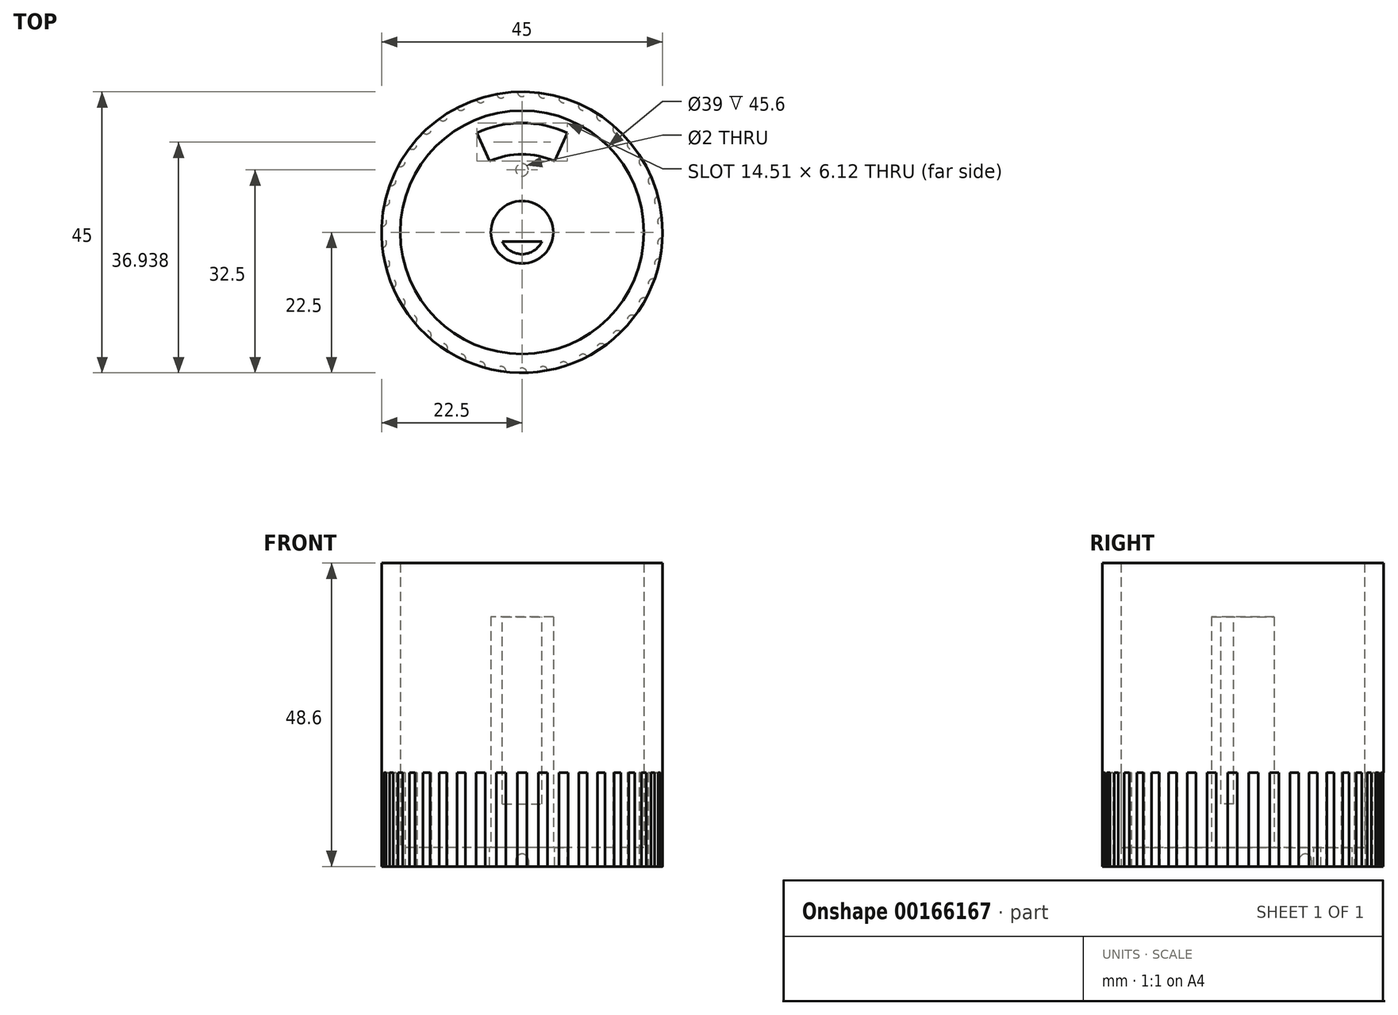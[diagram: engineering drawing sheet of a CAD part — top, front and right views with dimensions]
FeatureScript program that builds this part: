
annotation { "Feature Type Name" : "Feature", "Feature Type Description" : "" }
export const myFeature = defineFeature(function(context is Context, id is Id, definition is map)
    precondition{}
    {
        {
            var Q0;
            Q0=qCreatedBy(makeId("Top.planeOp"),FACE);
            var sketch = newSketch(context, id + "F10", { "sketchPlane" : qUnion([Q0])});
            skCircle(sketch, "E0", {"center": v(0, 0) * mm, "radius": 22.5 * mm});
            skSolve(sketch);
        }
        {
            var Q0;
            Q0=makeQuery(id+"F10.imprint","IMPRINT",FACE,{"disambiguationData":[TD([[makeQuery(id+"F10.imprint","IMPRINT",EDGE,{"derivedFrom":sQuery(id+"F10.wireOp",EDGE,"E0")}),1.0]])]});
            extrude(context, id + "F0", {"entities" : qUnion([Q0]), "depth" : 48.6 * mm});
        }
        {
            var Q0;
            Q0=makeQuery(id+"F0.opExtrude","CAP_FACE",FACE,{"disambiguationData":[OSD([sQuery(id+"F10.wireOp",EDGE,"E0")])],"isStart":false});
            shell(context, id + "F1", {"entities" : qUnion([Q0]), "thickness" : 3 * mm});
        }
        {
            var Q0;
            {var subQ0=sQuery(id+"F10.wireOp",EDGE,"E0");Q0=makeQuery(id+"F1.opShell","OFFSET_FACE",FACE,{"disambiguationData":[OSD([subQ0]),TDD([makeQuery(id+"F0.opExtrude","CAP_FACE",FACE,{"disambiguationData":[OSD([subQ0])],"isStart":true})])]});}
            var sketch = newSketch(context, id + "F2", { "sketchPlane" : qUnion([Q0])});
            skCircle(sketch, "E1", {"center": v(0, 0) * mm, "radius": 5 * mm});
            skSolve(sketch);
        }
        {
            var Q0;
            Q0 = qSketchRegion(id + "F2", true);
            extrude(context, id + "F3", {"entities" : qUnion([Q0]), "operationType" : NewBodyOperationType.ADD, "depth" : 37 * mm});
        }
        {
            var Q0;
            Q0=makeQuery(id+"F3.opExtrude","CAP_FACE",FACE,{"disambiguationData":[OSD([sQuery(id+"F2.wireOp",EDGE,"E1")])],"isStart":false});
            var sketch = newSketch(context, id + "F4", { "sketchPlane" : qUnion([Q0])});
            skCircle(sketch, "E2", {"center": v(0, 0) * mm, "radius": 3.5 * mm});
            skPoint(sketch, "E3", {"position": v(0, 3.5) * mm});
            skLineSegment(sketch, "E4", {"start": v(-3.9, -1.5) * mm, "end": v(4, -1.5) * mm});
            skSolve(sketch);
        }
        {
            var Q0;
            {var subQ0=sQuery(id+"F4.wireOp",EDGE,"E4");var subQ1=sQuery(id+"F4.wireOp",EDGE,"E2");var subQ2=makeQuery(id+"F4.imprint","INTERSECT",VERTEX,{"disambiguationData":[OD(0.0)],"derivedFrom":[subQ1,subQ0]});Q0=makeQuery(id+"F4.imprint","IMPRINT",FACE,{"disambiguationData":[TD([[makeQuery(id+"F4.imprint","IMPRINT",EDGE,{"disambiguationData":[TD([[subQ2,1.0]])],"derivedFrom":subQ1}),1.0]])]});}
            extrude(context, id + "F11", {"entities" : qUnion([Q0]), "operationType" : NewBodyOperationType.REMOVE, "oppositeDirection" : true, "depth" : 30 * mm});
        }
        {
            var Q0;
            {var subQ0=sQuery(id+"F10.wireOp",EDGE,"E0");Q0=makeQuery(id+"F1.opShell","OFFSET_FACE",FACE,{"disambiguationData":[OSD([subQ0]),TDD([makeQuery(id+"F0.opExtrude","CAP_FACE",FACE,{"disambiguationData":[OSD([subQ0])],"isStart":true})])]});}
            var sketch = newSketch(context, id + "F12", { "sketchPlane" : qUnion([Q0])});
            skCircle(sketch, "E5", {"center": v(0, 0) * mm, "radius": 17.5 * mm});
            skCircle(sketch, "E6", {"center": v(0, 0) * mm, "radius": 12.5 * mm});
            skLineSegment(sketch, "E7", {"start": v(0, 0) * mm, "end": v(7.26, 15.93) * mm});
            skLineSegment(sketch, "E8", {"start": v(0, 0) * mm, "end": v(-7.26, 15.93) * mm});
            skLineSegment(sketch, "E9", {"start": v(-7.26, 15.93) * mm, "end": v(7.26, 15.93) * mm});
            skSolve(sketch);
        }
        {
            var Q0;
            {var subQ5=sQuery(id+"F12.wireOp",EDGE,"E9");Q0=makeQuery(id+"F12.imprint","IMPRINT",FACE,{"disambiguationData":[TD([[makeQuery(id+"F12.imprint","IMPRINT",EDGE,{"derivedFrom":subQ5}),-1.0]])]});}
            var Q1;
            {var subQ0=sQuery(id+"F12.wireOp",EDGE,"E9");Q1=makeQuery(id+"F12.imprint","IMPRINT",FACE,{"disambiguationData":[TD([[makeQuery(id+"F12.imprint","IMPRINT",EDGE,{"derivedFrom":subQ0}),1.0]])]});}
            extrude(context, id + "F5", {"entities" : qUnion([Q0, Q1]), "operationType" : NewBodyOperationType.REMOVE, "oppositeDirection" : true, "depth" : 25 * mm});
        }
        {
            var Q0;
            Q0=makeQuery(id+"F0.opExtrude","CAP_FACE",FACE,{"disambiguationData":[OSD([sQuery(id+"F10.wireOp",EDGE,"E0")])],"isStart":true});
            var sketch = newSketch(context, id + "F13", { "sketchPlane" : qUnion([Q0])});
            skCircle(sketch, "E10", {"center": v(0, -10) * mm, "radius": 1 * mm});
            skSolve(sketch);
        }
        {
            var Q0;
            Q0=makeQuery(id+"F13.imprint","IMPRINT",FACE,{"disambiguationData":[TD([[makeQuery(id+"F13.imprint","IMPRINT",EDGE,{"derivedFrom":sQuery(id+"F13.wireOp",EDGE,"E10")}),1.0]])]});
            extrude(context, id + "F6", {"entities" : qUnion([Q0]), "operationType" : NewBodyOperationType.REMOVE, "oppositeDirection" : true, "depth" : 2 * mm});
        }
        {
            var Q0;
            Q0=makeQuery(id+"F6.boolean.opBoolean","COPY",EDGE,{"derivedFrom":makeQuery(id+"F6.opExtrude","CAP_EDGE",EDGE,{"disambiguationData":[OSD([sQuery(id+"F13.wireOp",EDGE,"E10")])],"isStart":false})});
            fillet(context, id + "F7", {"entities" : qUnion([Q0]), "radius" : 1 * mm, "tangentPropagation" : true, "allowEdgeOverflow" : false});
        }
        {
            var Q0;
            Q0=makeQuery(id+"F0.opExtrude","CAP_FACE",FACE,{"disambiguationData":[OSD([sQuery(id+"F10.wireOp",EDGE,"E0")])],"isStart":true});
            var sketch = newSketch(context, id + "F8", { "sketchPlane" : qUnion([Q0])});
            skCircle(sketch, "E11", {"center": v(0, -22.5) * mm, "radius": 0.75 * mm});
            skCircle(sketch, "E12.1.0", {"center": v(3.35, -22.25) * mm, "radius": 0.75 * mm});
            skCircle(sketch, "E12.2.0", {"center": v(6.63, -21.5) * mm, "radius": 0.75 * mm});
            skCircle(sketch, "E12.3.0", {"center": v(9.76, -20.27) * mm, "radius": 0.75 * mm});
            skCircle(sketch, "E12.4.0", {"center": v(12.67, -18.6) * mm, "radius": 0.75 * mm});
            skCircle(sketch, "E12.5.0", {"center": v(15.3, -16.5) * mm, "radius": 0.75 * mm});
            skCircle(sketch, "E12.6.0", {"center": v(17.6, -14.03) * mm, "radius": 0.75 * mm});
            skCircle(sketch, "E12.7.0", {"center": v(19.49, -11.25) * mm, "radius": 0.75 * mm});
            skCircle(sketch, "E12.8.0", {"center": v(20.94, -8.22) * mm, "radius": 0.75 * mm});
            skCircle(sketch, "E12.9.0", {"center": v(21.94, -5) * mm, "radius": 0.75 * mm});
            skCircle(sketch, "E12.10.0", {"center": v(22.44, -1.68) * mm, "radius": 0.75 * mm});
            skCircle(sketch, "E12.11.0", {"center": v(22.44, 1.68) * mm, "radius": 0.75 * mm});
            skCircle(sketch, "E12.12.0", {"center": v(21.94, 5) * mm, "radius": 0.75 * mm});
            skCircle(sketch, "E12.13.0", {"center": v(20.94, 8.22) * mm, "radius": 0.75 * mm});
            skCircle(sketch, "E12.14.0", {"center": v(19.49, 11.25) * mm, "radius": 0.75 * mm});
            skCircle(sketch, "E12.15.0", {"center": v(17.6, 14.03) * mm, "radius": 0.75 * mm});
            skCircle(sketch, "E12.16.0", {"center": v(15.3, 16.5) * mm, "radius": 0.75 * mm});
            skCircle(sketch, "E12.17.0", {"center": v(12.67, 18.6) * mm, "radius": 0.75 * mm});
            skCircle(sketch, "E12.18.0", {"center": v(9.76, 20.27) * mm, "radius": 0.75 * mm});
            skCircle(sketch, "E12.19.0", {"center": v(6.63, 21.5) * mm, "radius": 0.75 * mm});
            skCircle(sketch, "E12.20.0", {"center": v(3.35, 22.25) * mm, "radius": 0.75 * mm});
            skCircle(sketch, "E12.21.0", {"center": v(0, 22.5) * mm, "radius": 0.75 * mm});
            skCircle(sketch, "E12.22.0", {"center": v(-3.35, 22.25) * mm, "radius": 0.75 * mm});
            skCircle(sketch, "E12.23.0", {"center": v(-6.63, 21.5) * mm, "radius": 0.75 * mm});
            skCircle(sketch, "E12.24.0", {"center": v(-9.76, 20.27) * mm, "radius": 0.75 * mm});
            skCircle(sketch, "E12.25.0", {"center": v(-12.67, 18.6) * mm, "radius": 0.75 * mm});
            skCircle(sketch, "E12.26.0", {"center": v(-15.3, 16.5) * mm, "radius": 0.75 * mm});
            skCircle(sketch, "E12.27.0", {"center": v(-17.6, 14.03) * mm, "radius": 0.75 * mm});
            skCircle(sketch, "E12.28.0", {"center": v(-19.49, 11.25) * mm, "radius": 0.75 * mm});
            skCircle(sketch, "E12.29.0", {"center": v(-20.94, 8.22) * mm, "radius": 0.75 * mm});
            skCircle(sketch, "E12.30.0", {"center": v(-21.94, 5) * mm, "radius": 0.75 * mm});
            skCircle(sketch, "E12.31.0", {"center": v(-22.44, 1.68) * mm, "radius": 0.75 * mm});
            skCircle(sketch, "E12.32.0", {"center": v(-22.44, -1.68) * mm, "radius": 0.75 * mm});
            skCircle(sketch, "E12.33.0", {"center": v(-21.94, -5) * mm, "radius": 0.75 * mm});
            skCircle(sketch, "E12.34.0", {"center": v(-20.94, -8.22) * mm, "radius": 0.75 * mm});
            skCircle(sketch, "E12.35.0", {"center": v(-19.49, -11.25) * mm, "radius": 0.75 * mm});
            skCircle(sketch, "E12.36.0", {"center": v(-17.6, -14.03) * mm, "radius": 0.75 * mm});
            skCircle(sketch, "E12.37.0", {"center": v(-15.3, -16.5) * mm, "radius": 0.75 * mm});
            skCircle(sketch, "E12.38.0", {"center": v(-12.67, -18.6) * mm, "radius": 0.75 * mm});
            skCircle(sketch, "E12.39.0", {"center": v(-9.76, -20.27) * mm, "radius": 0.75 * mm});
            skCircle(sketch, "E12.40.0", {"center": v(-6.63, -21.5) * mm, "radius": 0.75 * mm});
            skCircle(sketch, "E12.41.0", {"center": v(-3.35, -22.25) * mm, "radius": 0.75 * mm});
            skPoint(sketch, "E12.center", {"position": v(0, 0) * mm});
            skSolve(sketch);
        }
        {
            var Q0;
            Q0 = qSketchRegion(id + "F8", true);
            extrude(context, id + "F9", {"entities" : qUnion([Q0]), "operationType" : NewBodyOperationType.REMOVE, "oppositeDirection" : true, "depth" : 15 * mm});
        }
    });
